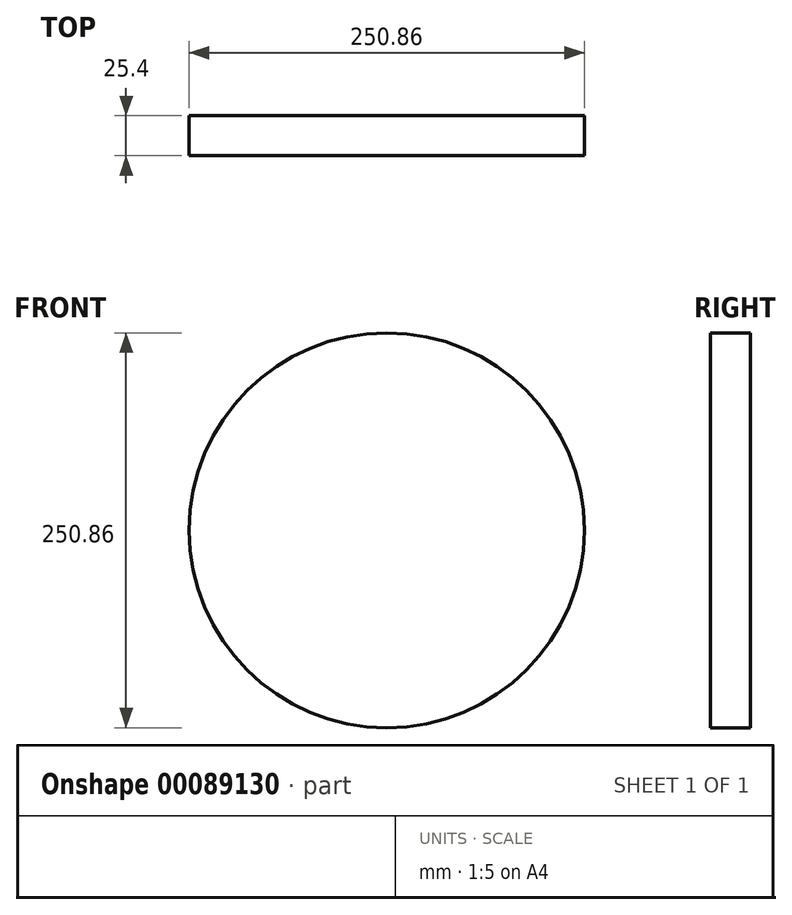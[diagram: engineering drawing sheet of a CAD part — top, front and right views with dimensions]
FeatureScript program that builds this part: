
annotation { "Feature Type Name" : "Feature", "Feature Type Description" : "" }
export const myFeature = defineFeature(function(context is Context, id is Id, definition is map)
    precondition{}
    {
        {
            var Q0;
            Q0=qCreatedBy(makeId("Front.planeOp"),FACE);
            var sketch = newSketch(context, id + "F0", { "sketchPlane" : qUnion([Q0])});
            skCircle(sketch, "E0", {"center": v(0, 0) * mm, "radius": 125.43 * mm});
            skSolve(sketch);
        }
        {
            var Q0;
            Q0 = qSketchRegion(id + "F0", true);
            extrude(context, id + "F1", {"entities" : qUnion([Q0]), "depth" : 25.4 * mm});
        }
    });
